# Revit family: WL3082
name_source: partatom
category: Communication Devices
revit_build: Autodesk Revit Architecture 2012 (Build: 20110309_2315(x64)
units: mm (PartAtom-declared; Revit-internal decimal feet)

## types (1)
- WL3082
    Coverage Horizontal = 140.00°
    Coverage Vertical = 10.00°
    Default Elevation = 0.000"
    Depth = 16.000"
    Description = Dual 8" Line Array Loudspeaker Element
    Enclosure Finish = Black Finish
    Enclosure Width = 19.900"
    Grill Finish = Black Grille
    Grill Front Height = 8.063"
    Grill Rear Offset = 0.750"
    Height = 9.000"
    Impedance = 16
    Impedance 2 = 16
    Impedance 3 = 16
    Manufacturer = QSC Audio Products, LLC
    Manufacturer URL = www.qscaudio.com
    Mid Section Rear Offset = 2.500"
    Model = WL3082
    Power Handling = 250
    Power Handling 2 = 250
    Power Handling 3 = 85
    Product Documentation Link = http://media.qscaudio.com
    Product Page URL = http://www.qscaudio.com
    Rear Height = 6.480"
    Rear Rigging Collision Zone Front Offset = 11.531"
    Rear Rigging Collision Zone Rear Offset = 15.311"
    Regulatory Compliance = RoHS
    Rigging Collision Zone Finish = Black Finish
    Rigging Collision Zone Width = 0.900"
    SPL Max = 127
    Sensitivity = 98
    Sensitivity 2 = 98
    Sensitivity 3 = 108
    URL = http://www.qscaudio.com
    Weight Dimensional (kg) = 20.7
    Weight Dimensional (lb) = 45.5
    Weight Product (kg) = 17
    Weight Product (lb) = 38
    Width = 21.700"

## geometry (parser evidence)
native form markers: Sweep x2
no freeform markers — native parametric forms only
